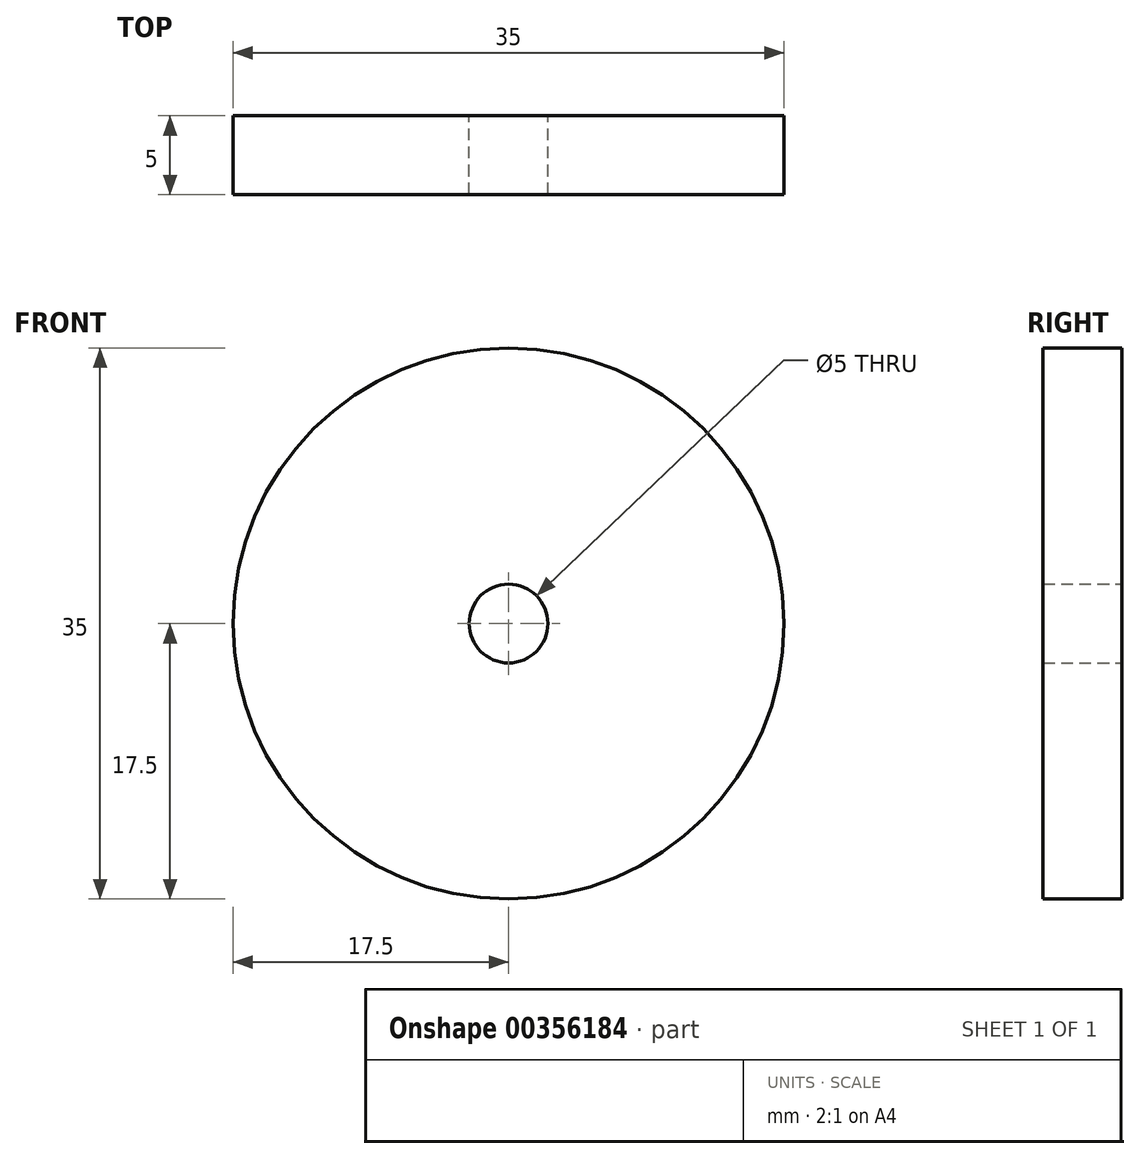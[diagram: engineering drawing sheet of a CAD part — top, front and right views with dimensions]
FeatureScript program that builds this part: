
annotation { "Feature Type Name" : "Feature", "Feature Type Description" : "" }
export const myFeature = defineFeature(function(context is Context, id is Id, definition is map)
    precondition{}
    {
        {
            var Q0;
            Q0=qCreatedBy(makeId("Front.planeOp"),FACE);
            var sketch = newSketch(context, id + "F0", { "sketchPlane" : qUnion([Q0])});
            skCircle(sketch, "E0", {"center": v(0, 0) * mm, "radius": 17.5 * mm});
            skCircle(sketch, "E1", {"center": v(0, 0) * mm, "radius": 2.5 * mm});
            skSolve(sketch);
        }
        {
            var Q0;
            Q0=makeQuery(id+"F0.imprint","IMPRINT",FACE,{"disambiguationData":[TD([[makeQuery(id+"F0.imprint","IMPRINT",EDGE,{"derivedFrom":sQuery(id+"F0.wireOp",EDGE,"E0")}),1.0]])]});
            extrude(context, id + "F1", {"entities" : qUnion([Q0]), "depth" : 5 * mm});
        }
    });
